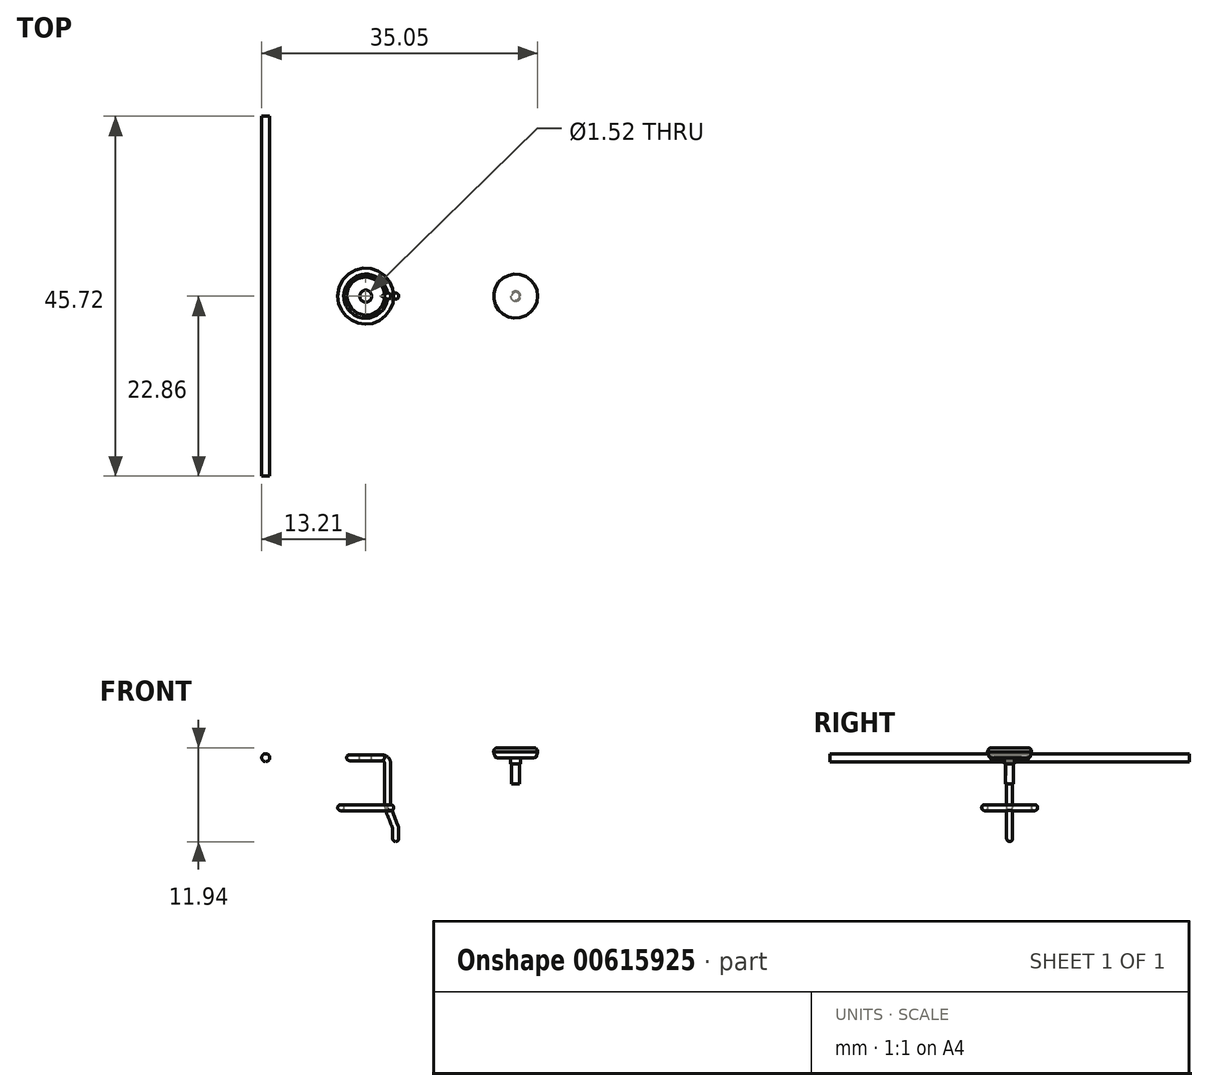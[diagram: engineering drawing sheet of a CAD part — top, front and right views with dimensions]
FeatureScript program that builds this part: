
annotation { "Feature Type Name" : "Feature", "Feature Type Description" : "" }
export const myFeature = defineFeature(function(context is Context, id is Id, definition is map)
    precondition{}
    {
        {
            var Q0;
            Q0=qCreatedBy(makeId("Top.planeOp"),FACE);
            var sketch = newSketch(context, id + "F0", { "sketchPlane" : qUnion([Q0])});
            skCircle(sketch, "E0", {"center": v(0, 0) * mm, "radius": 2.03 * mm});
            skSolve(sketch);
        }
        {
            var Q0;
            Q0=qCreatedBy(makeId("Front.planeOp"),FACE);
            var sketch = newSketch(context, id + "F1", { "sketchPlane" : qUnion([Q0])});
            skCircle(sketch, "E1", {"center": v(2.03, 0) * mm, "radius": 0.38 * mm});
            skSolve(sketch);
        }
        {
            var Q0;
            Q0 = qSketchRegion(id + "F1", true);
            var Q1;
            Q1 = qConstructionFilter(qBodyType(qCreatedBy(id + "F0" ,EDGE), BodyType.WIRE), ConstructionObject.NO);
            sweep(context, id + "F2", {"profiles" : qUnion([Q0]), "path" : qUnion([Q1])});
        }
        {
            var Q0;
            Q0=qCreatedBy(makeId("Front.planeOp"),FACE);
            var sketch = newSketch(context, id + "F3", { "sketchPlane" : qUnion([Q0])});
            skLineSegment(sketch, "E2", {"start": v(2.8, -0.76) * mm, "end": v(2.8, -6.1) * mm});
            skLineSegment(sketch, "E3", {"start": v(2.88, -6.58) * mm, "end": v(3.72, -8.66) * mm});
            skLineSegment(sketch, "E4", {"start": v(3.81, -9.13) * mm, "end": v(3.81, -10.67) * mm});
            skLineSegment(sketch, "E5", {"start": v(0, 0) * mm, "end": v(2.03, 0) * mm});
            skPoint(sketch, "E6.visualSharp", {"position": v(2.8, 0) * mm});
            skArc(sketch, "E6.filletArc", {"start": v(2.8, -0.76) * mm, "mid": v(2.57, -0.22) * mm, "end": v(2.03, 0) * mm});
            skPoint(sketch, "E7.visualSharp", {"position": v(2.8, -6.35) * mm});
            skArc(sketch, "E7.filletArc", {"start": v(2.8, -6.1) * mm, "mid": v(2.82, -6.35) * mm, "end": v(2.88, -6.58) * mm});
            skPoint(sketch, "E8.visualSharp", {"position": v(3.81, -8.9) * mm});
            skArc(sketch, "E8.filletArc", {"start": v(3.81, -9.13) * mm, "mid": v(3.79, -8.9) * mm, "end": v(3.72, -8.66) * mm});
            skSolve(sketch);
        }
        {
            var Q0;
            Q0=qCreatedBy(makeId("Right.planeOp"),FACE);
            var sketch = newSketch(context, id + "F4", { "sketchPlane" : qUnion([Q0])});
            skCircle(sketch, "E9", {"center": v(0, 0) * mm, "radius": 0.38 * mm});
            skSolve(sketch);
        }
        {
            var Q0;
            Q0 = qSketchRegion(id + "F4", true);
            var Q1;
            Q1 = qConstructionFilter(qBodyType(qCreatedBy(id + "F3" ,EDGE), BodyType.WIRE), ConstructionObject.NO);
            sweep(context, id + "F5", {"operationType" : NewBodyOperationType.ADD, "profiles" : qUnion([Q0]), "path" : qUnion([Q1])});
        }
        {
            var Q0;
            Q0=qCreatedBy(makeId("Top.planeOp"),FACE);
            cPlane(context, id + "F6", {"entities" : qUnion([Q0]), "cplaneType" : CPlaneType.OFFSET, "offset" : 6.35 * mm, "oppositeDirection" : true, "width" : 152.4 * mm, "height" : 152.4 * mm});
        }
        {
            var Q0;
            Q0=qCreatedBy(id+"F6.planeOp",FACE);
            var sketch = newSketch(context, id + "F7", { "sketchPlane" : qUnion([Q0])});
            skCircle(sketch, "E10", {"center": v(0, 0) * mm, "radius": 3.18 * mm});
            skSolve(sketch);
        }
        {
            var Q0;
            Q0=qCreatedBy(makeId("Front.planeOp"),FACE);
            var sketch = newSketch(context, id + "F8", { "sketchPlane" : qUnion([Q0])});
            skCircle(sketch, "E11", {"center": v(3.18, -6.35) * mm, "radius": 0.38 * mm});
            skSolve(sketch);
        }
        {
            var Q0;
            Q0 = qSketchRegion(id + "F8", true);
            var Q1;
            Q1 = qConstructionFilter(qBodyType(qCreatedBy(id + "F7" ,EDGE), BodyType.WIRE), ConstructionObject.NO);
            sweep(context, id + "F9", {"operationType" : NewBodyOperationType.ADD, "profiles" : qUnion([Q0]), "path" : qUnion([Q1])});
        }
        {
            var Q0;
            Q0 = qSketchRegion(id + "F0", true);
            extrude(context, id + "F10", {"entities" : qUnion([Q0]), "operationType" : NewBodyOperationType.ADD, "endBound" : BoundingType.SYMMETRIC, "oppositeDirection" : true, "depth" : 0.76 * mm, "offsetDistance" : 25.4 * mm});
        }
        {
            var Q0;
            Q0=makeQuery(id+"F10.opExtrude","CAP_FACE",FACE,{"disambiguationData":[OSD([sQuery(id+"F0.wireOp",EDGE,"E0")])],"isStart":true});
            var sketch = newSketch(context, id + "F11", { "sketchPlane" : qUnion([Q0])});
            skCircle(sketch, "E12", {"center": v(0, 0) * mm, "radius": 0.76 * mm});
            skSolve(sketch);
        }
        {
            var Q0;
            Q0 = qSketchRegion(id + "F11", true);
            extrude(context, id + "F12", {"entities" : qUnion([Q0]), "operationType" : NewBodyOperationType.REMOVE, "endBound" : BoundingType.UP_TO_NEXT, "oppositeDirection" : true, "depth" : 25.4 * mm, "offsetDistance" : 25.4 * mm});
        }
        {
            var Q0;
            Q0=qCreatedBy(makeId("Top.planeOp"),FACE);
            var sketch = newSketch(context, id + "F13", { "sketchPlane" : qUnion([Q0])});
            skCircle(sketch, "E13", {"center": v(19.05, 0) * mm, "radius": 2.8 * mm});
            skSolve(sketch);
        }
        {
            var Q0;
            Q0 = qSketchRegion(id + "F13", true);
            extrude(context, id + "F14", {"entities" : qUnion([Q0]), "depth" : 1.27 * mm, "offsetDistance" : 25.4 * mm});
        }
        {
            var Q0;
            Q0=makeQuery(id+"F14.opExtrude","CAP_FACE",FACE,{"disambiguationData":[OSD([sQuery(id+"F13.wireOp",EDGE,"E13")])],"isStart":true});
            var sketch = newSketch(context, id + "F15", { "sketchPlane" : qUnion([Q0])});
            skCircle(sketch, "E14", {"center": v(19.05, 0) * mm, "radius": 0.64 * mm});
            skSolve(sketch);
        }
        {
            var Q0;
            Q0=makeQuery(id+"F14.opExtrude","CAP_EDGE",EDGE,{"disambiguationData":[OSD([sQuery(id+"F13.wireOp",EDGE,"E13")])],"isStart":false});
            fillet(context, id + "F16", {"entities" : qUnion([Q0]), "radius" : 0.5 * mm, "tangentPropagation" : true, "allowEdgeOverflow" : false});
        }
        {
            var Q0;
            Q0=makeQuery(id+"F14.opExtrude","CAP_EDGE",EDGE,{"disambiguationData":[OSD([sQuery(id+"F13.wireOp",EDGE,"E13")])],"isStart":true});
            fillet(context, id + "F17", {"entities" : qUnion([Q0]), "radius" : 1.02 * mm, "tangentPropagation" : true, "rho" : .9, "crossSection" : FilletCrossSection.CONIC, "allowEdgeOverflow" : false});
        }
        {
            var Q0;
            Q0 = qSketchRegion(id + "F15", true);
            extrude(context, id + "F18", {"entities" : qUnion([Q0]), "operationType" : NewBodyOperationType.ADD, "depth" : 0.76 * mm, "offsetDistance" : 25.4 * mm});
        }
        {
            var Q0;
            Q0=makeQuery(id+"F5.opSweep","CAP_EDGE",EDGE,{"disambiguationData":[OSD([sQuery(id+"F3.wireOp",VERTEX,"E4.end"),sQuery(id+"F4.wireOp",EDGE,"E9")])],"isStart":false});
            var Q1;
            Q1=makeQuery(id+"Fs1Sru3lkXgNTJl_1.1.F5.opSweep","CAP_EDGE",EDGE,{"disambiguationData":[OSD([sQuery(id+"F3.wireOp",VERTEX,"E4.end"),sQuery(id+"F4.wireOp",EDGE,"E9")])],"isStart":false});
            var Q2;
            Q2=makeQuery(id+"Fs1Sru3lkXgNTJl_1.2.F5.opSweep","CAP_EDGE",EDGE,{"disambiguationData":[OSD([sQuery(id+"F3.wireOp",VERTEX,"E4.end"),sQuery(id+"F4.wireOp",EDGE,"E9")])],"isStart":false});
            var Q3;
            Q3=makeQuery(id+"Fs1Sru3lkXgNTJl_1.3.F5.opSweep","CAP_EDGE",EDGE,{"disambiguationData":[OSD([sQuery(id+"F3.wireOp",VERTEX,"E4.end"),sQuery(id+"F4.wireOp",EDGE,"E9")])],"isStart":false});
            fillet(context, id + "F19", {"entities" : qUnion([Q0, Q1, Q2, Q3]), "radius" : 0.38 * mm, "tangentPropagation" : true, "allowEdgeOverflow" : false});
        }
        {
            var Q0;
            Q0=makeQuery(id+"F18.opExtrude","CAP_FACE",FACE,{"disambiguationData":[OSD([sQuery(id+"F15.wireOp",EDGE,"E14")])],"isStart":false});
            var sketch = newSketch(context, id + "F20", { "sketchPlane" : qUnion([Q0])});
            skCircle(sketch, "E15", {"center": v(19.05, 0) * mm, "radius": 0.5 * mm});
            skSolve(sketch);
        }
        {
            var Q0;
            Q0 = qSketchRegion(id + "F20", true);
            extrude(context, id + "F21", {"entities" : qUnion([Q0]), "operationType" : NewBodyOperationType.ADD, "depth" : 2.54 * mm, "offsetDistance" : 25.4 * mm});
        }
        {
            var Q0;
            Q0=qCreatedBy(makeId("Front.planeOp"),FACE);
            var sketch = newSketch(context, id + "F22", { "sketchPlane" : qUnion([Q0])});
            skCircle(sketch, "E16", {"center": v(-12.7, 0) * mm, "radius": 0.5 * mm});
            skSolve(sketch);
        }
        {
            var Q0;
            Q0 = qSketchRegion(id + "F22", true);
            extrude(context, id + "F23", {"entities" : qUnion([Q0]), "endBound" : BoundingType.SYMMETRIC, "depth" : 45.72 * mm, "offsetDistance" : 25.4 * mm});
        }
    });
